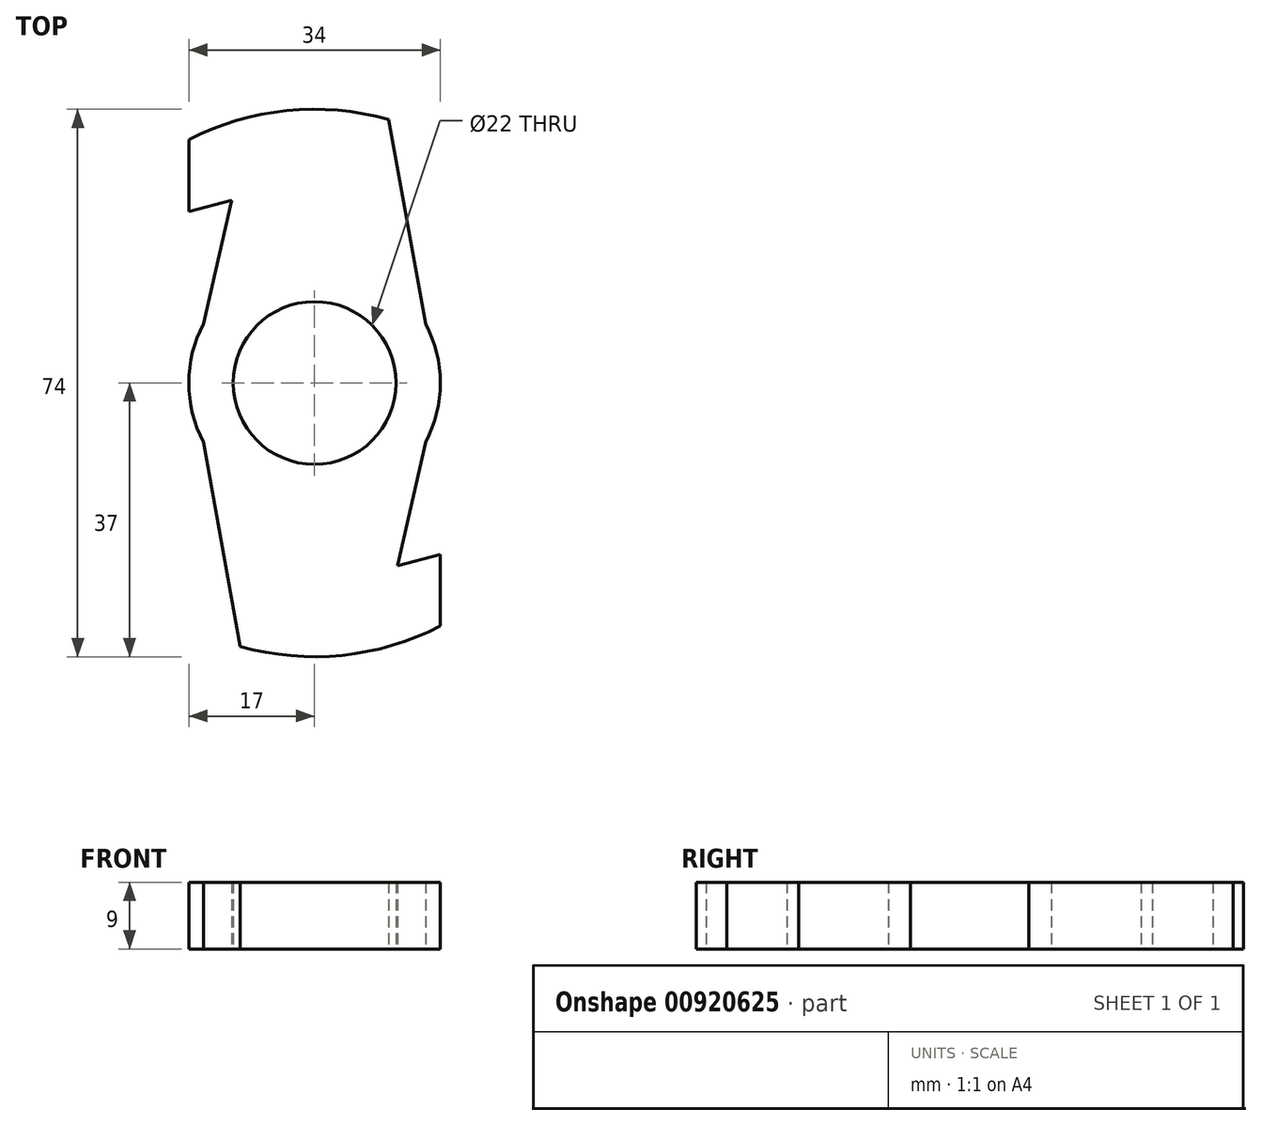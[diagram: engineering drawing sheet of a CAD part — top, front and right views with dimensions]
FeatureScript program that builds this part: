
annotation { "Feature Type Name" : "Feature", "Feature Type Description" : "" }
export const myFeature = defineFeature(function(context is Context, id is Id, definition is map)
    precondition{}
    {
        {
            var Q0;
            Q0=qCreatedBy(makeId("Top.planeOp"),FACE);
            var sketch = newSketch(context, id + "F0", { "sketchPlane" : qUnion([Q0])});
            skCircle(sketch, "E0", {"center": v(0, 0) * mm, "radius": 11 * mm});
            skLineSegment(sketch, "E1", {"start": v(-17, 32.86) * mm, "end": v(-17, 23.16) * mm});
            skLineSegment(sketch, "E2", {"start": v(-17, 23.16) * mm, "end": v(-11.2, 24.71) * mm});
            skLineSegment(sketch, "E3", {"start": v(-11.2, 24.71) * mm, "end": v(-15, 8) * mm});
            skLineSegment(sketch, "E4", {"start": v(10.03, 35.62) * mm, "end": v(15, 8) * mm});
            skLineSegment(sketch, "E5", {"start": v(-15, 8) * mm, "end": v(15, 8) * mm, "construction": true});
            skArc(sketch, "E6", {"start": v(10.03, 35.62) * mm, "mid": v(-3.75, 36.8) * mm, "end": v(-17, 32.86) * mm});
            skArc(sketch, "E7", {"start": v(15, 8) * mm, "mid": v(0, 17) * mm, "end": v(-15, 8) * mm, "construction": true});
            skArc(sketch, "E8", {"start": v(-15, 8) * mm, "mid": v(-16.5, 4.12) * mm, "end": v(-17, 0) * mm});
            skArc(sketch, "E9", {"start": v(17, 0) * mm, "mid": v(16.5, 4.12) * mm, "end": v(15, 8) * mm});
            skArc(sketch, "E10.1.0", {"start": v(15, -8) * mm, "mid": v(16.5, -4.12) * mm, "end": v(17, 0) * mm});
            skLineSegment(sketch, "E10.1.1", {"start": v(11.2, -24.71) * mm, "end": v(15, -8) * mm});
            skArc(sketch, "E10.1.2", {"start": v(-15, -8) * mm, "mid": v(0, -17) * mm, "end": v(15, -8) * mm, "construction": true});
            skLineSegment(sketch, "E10.1.3", {"start": v(15, -8) * mm, "end": v(-15, -8) * mm, "construction": true});
            skLineSegment(sketch, "E10.1.4", {"start": v(17, -23.16) * mm, "end": v(11.2, -24.71) * mm});
            skLineSegment(sketch, "E10.1.5", {"start": v(17, -32.86) * mm, "end": v(17, -23.16) * mm});
            skArc(sketch, "E10.1.6", {"start": v(-10.03, -35.62) * mm, "mid": v(3.75, -36.8) * mm, "end": v(17, -32.86) * mm});
            skLineSegment(sketch, "E10.1.7", {"start": v(-10.03, -35.62) * mm, "end": v(-15, -8) * mm});
            skArc(sketch, "E10.1.8", {"start": v(-17, 0) * mm, "mid": v(-16.5, -4.12) * mm, "end": v(-15, -8) * mm});
            skSolve(sketch);
        }
        {
            var Q0;
            Q0=makeQuery(id+"F0.imprint","IMPRINT",FACE,{"disambiguationData":[TD([[makeQuery(id+"F0.imprint","IMPRINT",EDGE,{"derivedFrom":sQuery(id+"F0.wireOp",EDGE,"E0")}),-1.0]])]});
            extrude(context, id + "F1", {"entities" : qUnion([Q0]), "depth" : 9 * mm, "offsetDistance" : 25 * mm});
        }
    });
